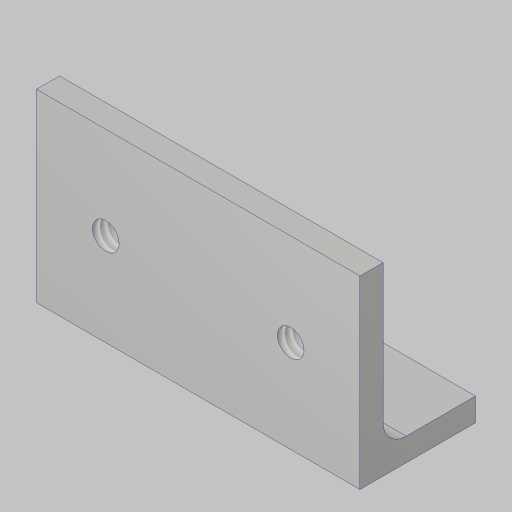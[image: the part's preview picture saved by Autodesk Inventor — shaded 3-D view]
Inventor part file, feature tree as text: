
AUTODESK INVENTOR PART (.ipt)
format: ipt  version: 2023.5 (Build 275446000, 446)  size: 137,728 bytes
history: native  units: in
note: dims shown in document units (in); Inventor stores cm internally (conversion verified against a paired STEP export)
features: sketch x3, hole x2, extrude x1, fillet x1
ambient origin geometry x8: Origin, YZ Plane, XZ Plane, XY Plane, X Axis, Y Axis, Z Axis, Center Point
bodies: Solid1 (feature_tree)
feature tree (7):
  extrude  "Extrusion1"  Depth=0.125in
  fillet  "Fillet1"  Radius=1.75in
  hole  "Hole1"  [1 undecoded]
  hole  "Hole2"  [1 undecoded]
  sketch  "Sketch1"  dims[d0=1.0in d2=0.125in d3=1.75in d4=0.0in]
  sketch  "Sketch2"  dims[d5=0.125in d6=0.25in]
  sketch  "Sketch3"  dims[d7=1.2598in d8=0.104in d9=0.276in d10=0.119in d11=0.25in d12=0.5635in d13=1.0in d14=0.8108in d15=1.0in d21=0.625in d22=0.5in d23=0.145in d24=0.38in d25=0.375in d26=0.25in d27=0.5635in d28=1.0in d29=0.8108in]
note: 2 required parameter values undecoded (feature->parameter linkage not recoverable at this tier; creation-order binding heuristic only, values carry confidence <= 0.55)
